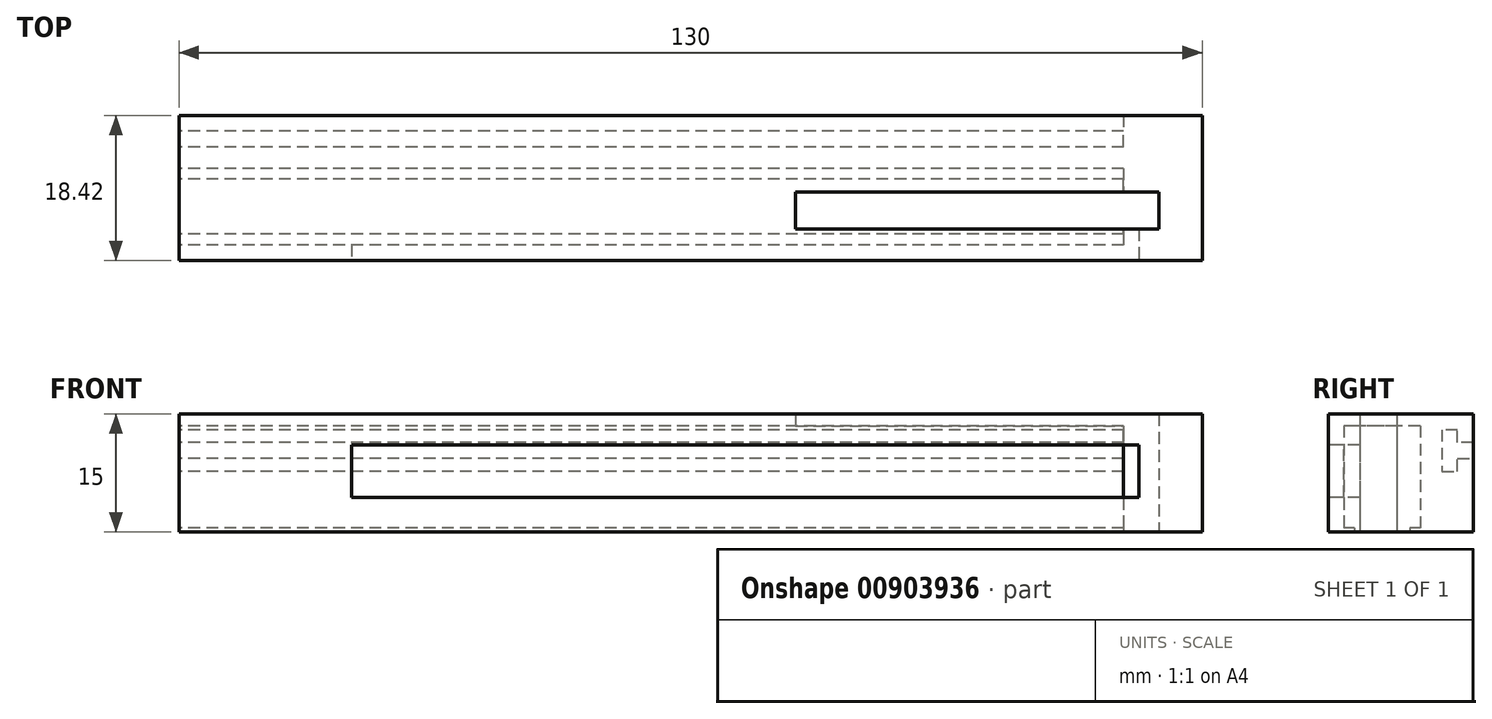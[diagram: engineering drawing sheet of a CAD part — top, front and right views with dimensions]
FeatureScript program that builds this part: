
annotation { "Feature Type Name" : "Feature", "Feature Type Description" : "" }
export const myFeature = defineFeature(function(context is Context, id is Id, definition is map)
    precondition{}
    {
        {
            var Q0;
            Q0=qCreatedBy(makeId("Top.planeOp"),FACE);
            var sketch = newSketch(context, id + "F0", { "sketchPlane" : qUnion([Q0])});
            skLineSegment(sketch, "E0.bottom", {"start": v(65, -9.22) * mm, "end": v(-65, -9.22) * mm});
            skLineSegment(sketch, "E0.top", {"start": v(65, 9.21) * mm, "end": v(-65, 9.21) * mm});
            skLineSegment(sketch, "E0.left", {"start": v(65, -9.22) * mm, "end": v(65, 9.21) * mm});
            skLineSegment(sketch, "E0.right", {"start": v(-65, -9.22) * mm, "end": v(-65, 9.21) * mm});
            skPoint(sketch, "E0.middle", {"position": v(0, 0) * mm});
            skLineSegment(sketch, "E1.bottom", {"start": v(59.5, -5.22) * mm, "end": v(13.32, -5.22) * mm});
            skLineSegment(sketch, "E1.top", {"start": v(59.5, -0.49) * mm, "end": v(13.32, -0.49) * mm});
            skLineSegment(sketch, "E1.left", {"start": v(59.5, -5.22) * mm, "end": v(59.5, -0.49) * mm});
            skLineSegment(sketch, "E1.right", {"start": v(13.32, -5.22) * mm, "end": v(13.32, -0.49) * mm});
            skSolve(sketch);
        }
        {
            var Q0;
            Q0=makeQuery(id+"F0.imprint","IMPRINT",FACE,{"disambiguationData":[TD([[makeQuery(id+"F0.imprint","IMPRINT",EDGE,{"derivedFrom":sQuery(id+"F0.wireOp",EDGE,"E0.bottom")}),-1.0]])]});
            extrude(context, id + "F1", {"entities" : qUnion([Q0]), "depth" : 15 * mm, "offsetDistance" : 25 * mm});
        }
        {
            var Q0;
            Q0=makeQuery(id+"F1.opExtrude","SWEPT_FACE",FACE,{"disambiguationData":[OSD([sQuery(id+"F0.wireOp",EDGE,"E0.right")])]});
            var sketch = newSketch(context, id + "F2", { "sketchPlane" : qUnion([Q0])});
            skLineSegment(sketch, "E2.bottom", {"start": v(-2.48, 13.5) * mm, "end": v(7.22, 13.5) * mm});
            skLineSegment(sketch, "E2.left", {"start": v(-2.48, 13.5) * mm, "end": v(-2.48, 0.5) * mm});
            skLineSegment(sketch, "E2.right", {"start": v(7.22, 13.5) * mm, "end": v(7.22, 0.5) * mm});
            skLineSegment(sketch, "E3.left", {"start": v(-1.13, 0.5) * mm, "end": v(-1.14, 0) * mm});
            skLineSegment(sketch, "E4", {"start": v(-9.21, 11.35) * mm, "end": v(-7.21, 11.35) * mm});
            skLineSegment(sketch, "E5", {"start": v(-7.21, 11.35) * mm, "end": v(-7.21, 13) * mm});
            skLineSegment(sketch, "E6", {"start": v(-7.21, 13) * mm, "end": v(-5.21, 13) * mm});
            skLineSegment(sketch, "E7", {"start": v(-5.21, 13) * mm, "end": v(-5.21, 7.7) * mm});
            skLineSegment(sketch, "E8", {"start": v(-5.21, 7.7) * mm, "end": v(-7.21, 7.7) * mm});
            skLineSegment(sketch, "E9", {"start": v(-7.21, 7.7) * mm, "end": v(-7.21, 9.35) * mm});
            skLineSegment(sketch, "E10", {"start": v(-7.21, 9.35) * mm, "end": v(-9.21, 9.35) * mm});
            skLineSegment(sketch, "E11", {"start": v(-9.21, 9.35) * mm, "end": v(-9.21, 11.35) * mm});
            skLineSegment(sketch, "E12.bottom", {"start": v(-1.13, 0.5) * mm, "end": v(5.87, 0.5) * mm});
            skLineSegment(sketch, "E12.top", {"start": v(-1.13, 0) * mm, "end": v(5.87, 0) * mm});
            skLineSegment(sketch, "E12.left", {"start": v(-1.13, 0.5) * mm, "end": v(-1.13, 0) * mm});
            skLineSegment(sketch, "E12.right", {"start": v(5.87, 0.5) * mm, "end": v(5.87, 0) * mm});
            skLineSegment(sketch, "E13", {"start": v(-2.48, 0.5) * mm, "end": v(-1.13, 0.5) * mm});
            skLineSegment(sketch, "E14", {"start": v(5.87, 0.5) * mm, "end": v(7.22, 0.5) * mm});
            skSolve(sketch);
        }
        {
            var Q0;
            Q0 = qSketchRegion(id + "F2", true);
            extrude(context, id + "F3", {"entities" : qUnion([Q0]), "operationType" : NewBodyOperationType.REMOVE, "oppositeDirection" : true, "depth" : 120 * mm, "offsetDistance" : 25 * mm});
        }
        {
            var Q0;
            Q0=makeQuery(id+"F1.opExtrude","SWEPT_FACE",FACE,{"disambiguationData":[OSD([sQuery(id+"F0.wireOp",EDGE,"E0.bottom")])]});
            var sketch = newSketch(context, id + "F4", { "sketchPlane" : qUnion([Q0])});
            skLineSegment(sketch, "E15.bottom", {"start": v(-43.06, 11.1) * mm, "end": v(56.94, 11.1) * mm});
            skLineSegment(sketch, "E15.top", {"start": v(-43.06, 4.41) * mm, "end": v(56.94, 4.41) * mm});
            skLineSegment(sketch, "E15.left", {"start": v(-43.06, 11.1) * mm, "end": v(-43.06, 4.41) * mm});
            skLineSegment(sketch, "E15.right", {"start": v(56.94, 11.1) * mm, "end": v(56.94, 4.41) * mm});
            skLineSegment(sketch, "E16", {"start": v(-43.06, 11.1) * mm, "end": v(-43.06, 15) * mm});
            skLineSegment(sketch, "E17", {"start": v(-43.06, 4.41) * mm, "end": v(-43.06, 0) * mm});
            skSolve(sketch);
        }
        {
            var Q0;
            Q0 = qSketchRegion(id + "F4", true);
            extrude(context, id + "F5", {"entities" : qUnion([Q0]), "operationType" : NewBodyOperationType.REMOVE, "oppositeDirection" : true, "depth" : 5 * mm, "offsetDistance" : 25 * mm});
        }
    });
